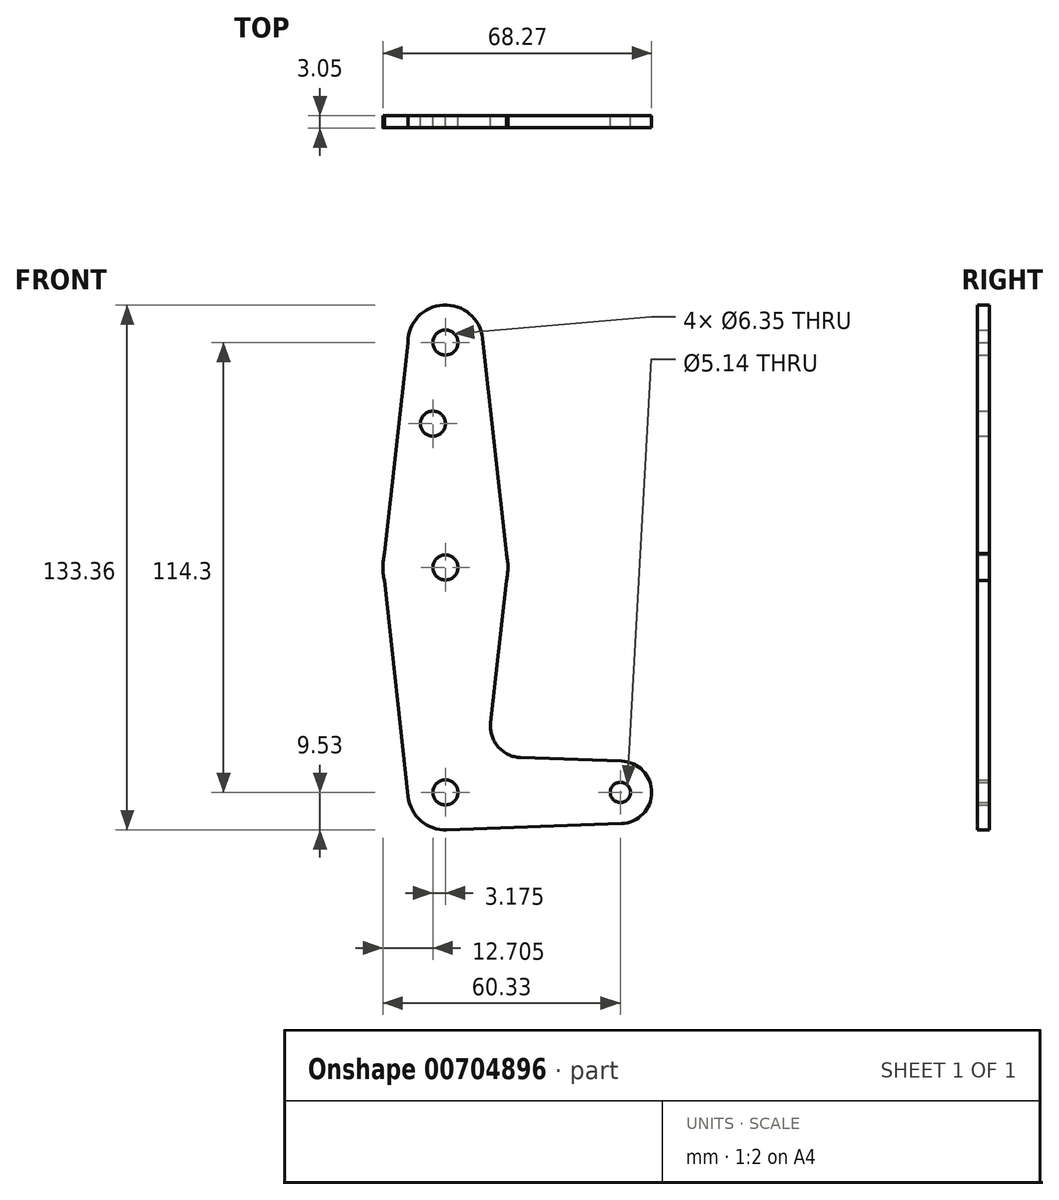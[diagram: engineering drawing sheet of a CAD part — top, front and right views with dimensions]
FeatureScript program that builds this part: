
annotation { "Feature Type Name" : "Feature", "Feature Type Description" : "" }
export const myFeature = defineFeature(function(context is Context, id is Id, definition is map)
    precondition{}
    {
        {
            var Q0;
            Q0=qCreatedBy(makeId("Front.planeOp"),FACE);
            var sketch = newSketch(context, id + "F0", { "sketchPlane" : qUnion([Q0])});
            skLineSegment(sketch, "E0", {"start": v(0, 114.3) * mm, "end": v(0, 0) * mm});
            skCircle(sketch, "E1", {"center": v(0, 114.3) * mm, "radius": 9.53 * mm});
            skCircle(sketch, "E2", {"center": v(0, 57.15) * mm, "radius": 15.88 * mm});
            skCircle(sketch, "E3", {"center": v(0, 0) * mm, "radius": 9.53 * mm});
            skLineSegment(sketch, "E4", {"start": v(0, 0) * mm, "end": v(44.45, 0) * mm});
            skCircle(sketch, "E5", {"center": v(44.45, 0) * mm, "radius": 7.94 * mm});
            skLineSegment(sketch, "E6", {"start": v(-9.53, 114.3) * mm, "end": v(-15.87, 57.01) * mm});
            skLineSegment(sketch, "E7", {"start": v(9.47, 115.34) * mm, "end": v(15.87, 56.99) * mm});
            skLineSegment(sketch, "E8", {"start": v(15.87, 56.99) * mm, "end": v(11.5, 17.67) * mm});
            skLineSegment(sketch, "E9", {"start": v(-15.87, 57.01) * mm, "end": v(-9.47, -1.04) * mm});
            skLineSegment(sketch, "E10", {"start": v(19.11, 8.84) * mm, "end": v(44.73, 7.93) * mm});
            skLineSegment(sketch, "E11", {"start": v(44.7, -7.93) * mm, "end": v(0, -9.53) * mm});
            skCircle(sketch, "E12", {"center": v(-3.18, 93.68) * mm, "radius": 3.18 * mm});
            skCircle(sketch, "E13", {"center": v(0, 57.15) * mm, "radius": 3.18 * mm});
            skCircle(sketch, "E14", {"center": v(0, 0) * mm, "radius": 3.18 * mm});
            skCircle(sketch, "E15", {"center": v(44.45, 0) * mm, "radius": 2.57 * mm});
            skCircle(sketch, "E16", {"center": v(0, 114.3) * mm, "radius": 3.18 * mm});
            skArc(sketch, "E17.filletArc", {"start": v(11.5, 17.67) * mm, "mid": v(13.38, 11.6) * mm, "end": v(19.11, 8.84) * mm});
            skSolve(sketch);
        }
        {
            var Q0;
            Q0 = qSketchRegion(id + "F0", true);
            var Q1;
            {var subQ0=sQuery(id+"F0.wireOp",EDGE,"E3");var subQ1=sQuery(id+"F0.wireOp",EDGE,"E0");var subQ2=makeQuery(id+"F0.imprint","INTERSECT",VERTEX,{"derivedFrom":[subQ1,subQ0]});Q1=makeQuery(id+"F0.imprint","IMPRINT",FACE,{"disambiguationData":[TD([[makeQuery(id+"F0.imprint","IMPRINT",EDGE,{"disambiguationData":[TD([[subQ2,-1.0]])],"derivedFrom":subQ1}),1.0]])]});}
            extrude(context, id + "F1", {"entities" : qUnion([Q0, Q1]), "depth" : 3.05 * mm, "offsetDistance" : 25.4 * mm});
        }
    });
